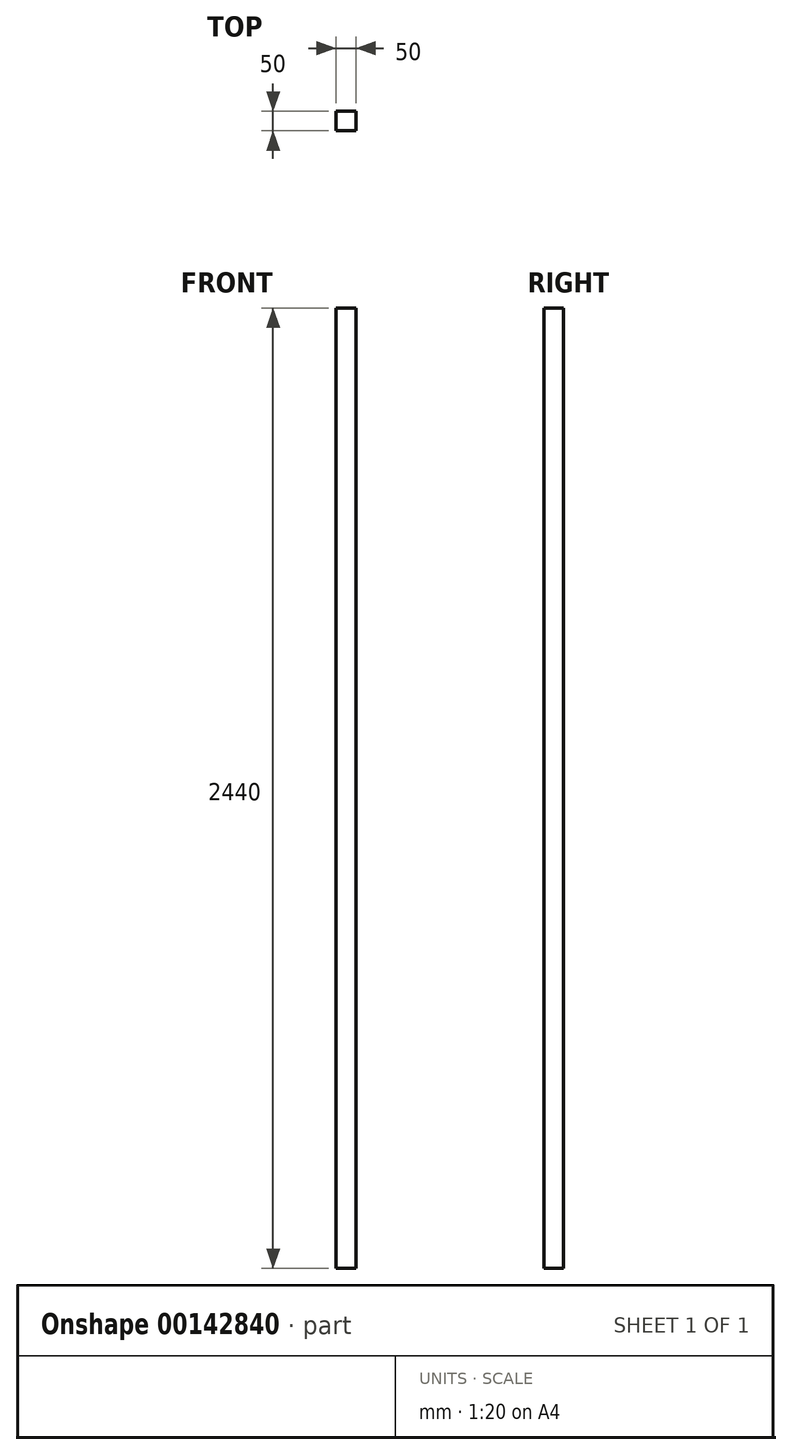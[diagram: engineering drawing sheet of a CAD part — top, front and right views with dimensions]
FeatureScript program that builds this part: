
annotation { "Feature Type Name" : "Feature", "Feature Type Description" : "" }
export const myFeature = defineFeature(function(context is Context, id is Id, definition is map)
    precondition{}
    {
        {
            var Q0;
            Q0=qCreatedBy(makeId("Front.planeOp"),FACE);
            var sketch = newSketch(context, id + "F0", { "sketchPlane" : qUnion([Q0])});
            skLineSegment(sketch, "E0.bottom", {"start": v(0, 0) * mm, "end": v(50, 0) * mm});
            skLineSegment(sketch, "E0.top", {"start": v(0, 2440) * mm, "end": v(50, 2440) * mm});
            skLineSegment(sketch, "E0.left", {"start": v(0, 0) * mm, "end": v(0, 2440) * mm});
            skLineSegment(sketch, "E0.right", {"start": v(50, 0) * mm, "end": v(50, 2440) * mm});
            skSolve(sketch);
        }
        {
            var Q0;
            Q0=qSketchRegion(id+"F0",true);
            extrude(context, id + "F1", {"entities" : qUnion([Q0]), "depth" : (50) * mm});
        }
    });
